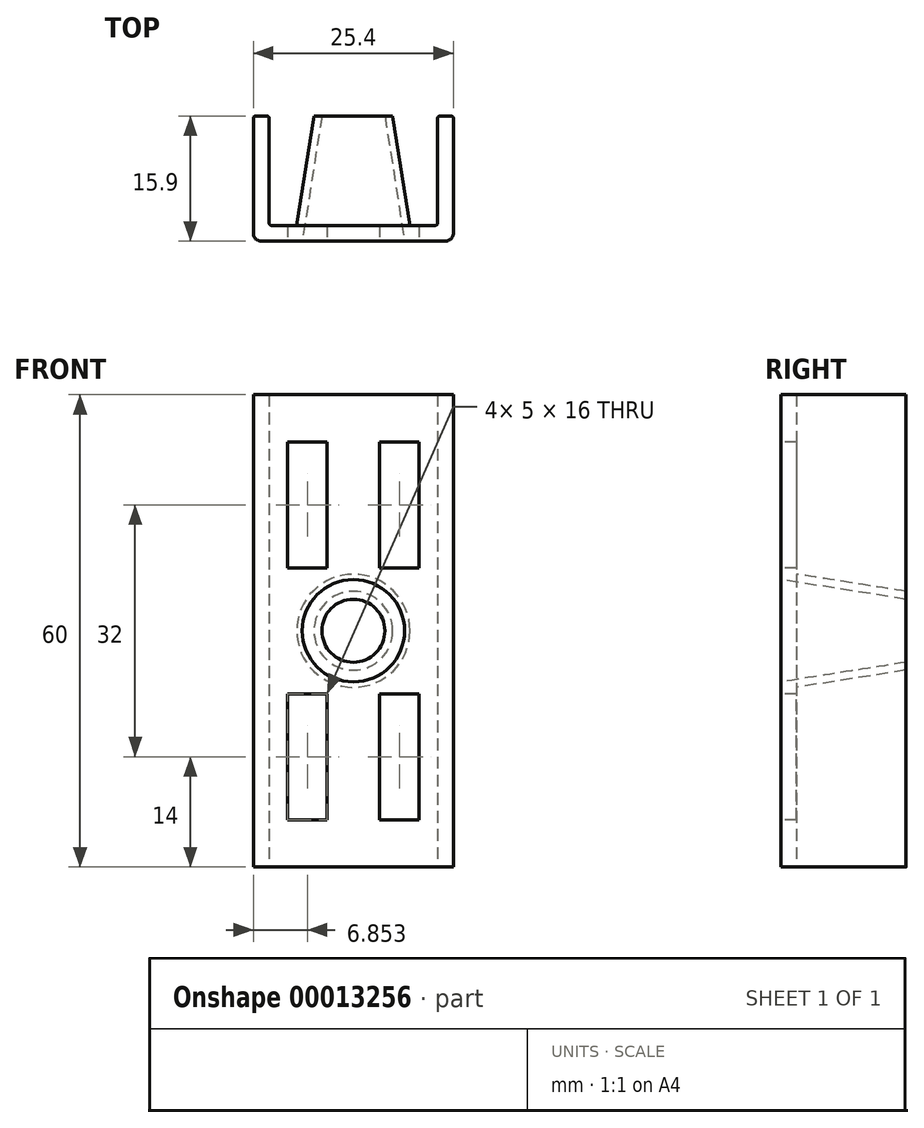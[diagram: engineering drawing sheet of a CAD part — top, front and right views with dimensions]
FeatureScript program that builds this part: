
annotation { "Feature Type Name" : "Feature", "Feature Type Description" : "" }
export const myFeature = defineFeature(function(context is Context, id is Id, definition is map)
    precondition{}
    {
        {
            var Q0;
            Q0=qCreatedBy(makeId("Top.planeOp"),FACE);
            var sketch = newSketch(context, id + "F0", { "sketchPlane" : qUnion([Q0])});
            skLineSegment(sketch, "E0.bottom", {"start": v(2.94, 36.07) * mm, "end": v(4.94, 36.07) * mm});
            skLineSegment(sketch, "E0.top", {"start": v(3.94, 20.17) * mm, "end": v(27.34, 20.17) * mm});
            skLineSegment(sketch, "E0.left", {"start": v(2.94, 36.07) * mm, "end": v(2.94, 21.17) * mm});
            skLineSegment(sketch, "E0.right", {"start": v(28.34, 36.07) * mm, "end": v(28.34, 21.17) * mm});
            skPoint(sketch, "E1.visualSharp", {"position": v(2.94, 20.17) * mm});
            skArc(sketch, "E1.filletArc", {"start": v(2.94, 21.17) * mm, "mid": v(3.24, 20.46) * mm, "end": v(3.94, 20.17) * mm});
            skPoint(sketch, "E2.visualSharp", {"position": v(28.34, 20.17) * mm});
            skArc(sketch, "E2.filletArc", {"start": v(27.34, 20.17) * mm, "mid": v(28.05, 20.46) * mm, "end": v(28.34, 21.17) * mm});
            skLineSegment(sketch, "E3.0", {"start": v(26.34, 36.07) * mm, "end": v(26.34, 22.17) * mm});
            skLineSegment(sketch, "E3.1", {"start": v(4.94, 22.17) * mm, "end": v(26.34, 22.17) * mm});
            skLineSegment(sketch, "E3.2", {"start": v(4.94, 36.07) * mm, "end": v(4.94, 22.17) * mm});
            skLineSegment(sketch, "E4.trimOffspring", {"start": v(26.34, 36.07) * mm, "end": v(28.34, 36.07) * mm});
            skSolve(sketch);
        }
        {
            var Q0;
            Q0=makeQuery(id+"F0.imprint","IMPRINT",FACE,{"disambiguationData":[TD([[makeQuery(id+"F0.imprint","IMPRINT",EDGE,{"derivedFrom":sQuery(id+"F0.wireOp",EDGE,"E0.bottom")}),-1.0]])]});
            extrude(context, id + "F1", {"entities" : qUnion([Q0]), "depth" : 60 * mm});
        }
        {
            var Q0;
            Q0=makeQuery(id+"F1.opExtrude","SWEPT_FACE",FACE,{"disambiguationData":[OSD([sQuery(id+"F0.wireOp",EDGE,"E0.top")])]});
            var sketch = newSketch(context, id + "F2", { "sketchPlane" : qUnion([Q0])});
            skLineSegment(sketch, "E5", {"start": v(15.64, 60) * mm, "end": v(15.64, 0) * mm, "construction": true});
            skLineSegment(sketch, "E6.bottom", {"start": v(19, 22) * mm, "end": v(24, 22) * mm});
            skLineSegment(sketch, "E6.top", {"start": v(19, 6) * mm, "end": v(24, 6) * mm});
            skLineSegment(sketch, "E6.left", {"start": v(19, 22) * mm, "end": v(19, 6) * mm});
            skLineSegment(sketch, "E6.right", {"start": v(24, 22) * mm, "end": v(24, 6) * mm});
            skLineSegment(sketch, "E7", {"start": v(15.64, 30) * mm, "end": v(27.34, 30) * mm, "construction": true});
            skLineSegment(sketch, "E8.0", {"start": v(15.64, 22) * mm, "end": v(27.34, 22) * mm, "construction": true});
            skPoint(sketch, "E9", {"position": v(21.5, 22) * mm});
            skLineSegment(sketch, "E10.0.MirrorCS", {"start": v(12.3, 22) * mm, "end": v(12.3, 6) * mm});
            skLineSegment(sketch, "E11.0.MirrorCS", {"start": v(7.3, 22) * mm, "end": v(7.3, 6) * mm});
            skLineSegment(sketch, "E12.0.MirrorCS", {"start": v(12.3, 22) * mm, "end": v(7.3, 22) * mm});
            skLineSegment(sketch, "E13.0.MirrorCS", {"start": v(12.3, 6) * mm, "end": v(7.3, 6) * mm});
            skLineSegment(sketch, "E14.0.MirrorCS", {"start": v(19, 38) * mm, "end": v(24, 38) * mm});
            skLineSegment(sketch, "E15.0.MirrorCS", {"start": v(24, 38) * mm, "end": v(24, 54) * mm});
            skLineSegment(sketch, "E16.0.MirrorCS", {"start": v(19, 38) * mm, "end": v(19, 54) * mm});
            skLineSegment(sketch, "E17.0.MirrorCS", {"start": v(19, 54) * mm, "end": v(24, 54) * mm});
            skLineSegment(sketch, "E18.0.MirrorCS", {"start": v(12.3, 38) * mm, "end": v(7.3, 38) * mm});
            skLineSegment(sketch, "E19.0.MirrorCS", {"start": v(12.3, 38) * mm, "end": v(12.3, 54) * mm});
            skLineSegment(sketch, "E20.0.MirrorCS", {"start": v(12.3, 54) * mm, "end": v(7.3, 54) * mm});
            skLineSegment(sketch, "E21.0.MirrorCS", {"start": v(7.3, 38) * mm, "end": v(7.3, 54) * mm});
            skCircle(sketch, "E22", {"center": v(15.64, 30) * mm, "radius": 7.5 * mm});
            skSolve(sketch);
        }
        {
            var Q0;
            Q0=makeQuery(id+"F2.imprint","IMPRINT",FACE,{"disambiguationData":[TD([[makeQuery(id+"F2.imprint","IMPRINT",EDGE,{"derivedFrom":sQuery(id+"F2.wireOp",EDGE,"E18.0.MirrorCS")}),-1.0]])]});
            var Q1;
            Q1=makeQuery(id+"F2.imprint","IMPRINT",FACE,{"disambiguationData":[TD([[makeQuery(id+"F2.imprint","IMPRINT",EDGE,{"derivedFrom":sQuery(id+"F2.wireOp",EDGE,"E14.0.MirrorCS")}),1.0]])]});
            var Q2;
            Q2=makeQuery(id+"F2.imprint","IMPRINT",FACE,{"disambiguationData":[TD([[makeQuery(id+"F2.imprint","IMPRINT",EDGE,{"derivedFrom":sQuery(id+"F2.wireOp",EDGE,"E6.bottom")}),-1.0]])]});
            var Q3;
            Q3=makeQuery(id+"F2.imprint","IMPRINT",FACE,{"disambiguationData":[TD([[makeQuery(id+"F2.imprint","IMPRINT",EDGE,{"derivedFrom":sQuery(id+"F2.wireOp",EDGE,"E10.0.MirrorCS")}),-1.0]])]});
            extrude(context, id + "F3", {"entities" : qUnion([Q0, Q1, Q2, Q3]), "operationType" : NewBodyOperationType.REMOVE, "oppositeDirection" : true, "depth" : 5 * mm});
        }
        {
            var Q0;
            Q0=makeQuery(id+"F1.opExtrude","SWEPT_EDGE",EDGE,{"disambiguationData":[OSD([sQuery(id+"F0.wireOp",EDGE,"E0.bottom"),sQuery(id+"F0.wireOp",EDGE,"E0.left")])]});
            var Q1;
            Q1=makeQuery(id+"F1.opExtrude","SWEPT_EDGE",EDGE,{"disambiguationData":[OSD([sQuery(id+"F0.wireOp",EDGE,"E0.bottom"),sQuery(id+"F0.wireOp",EDGE,"E3.2")])]});
            var Q2;
            Q2=makeQuery(id+"F1.opExtrude","SWEPT_EDGE",EDGE,{"disambiguationData":[OSD([sQuery(id+"F0.wireOp",EDGE,"E3.0"),sQuery(id+"F0.wireOp",EDGE,"E4.trimOffspring")])]});
            var Q3;
            Q3=makeQuery(id+"F1.opExtrude","SWEPT_EDGE",EDGE,{"disambiguationData":[OSD([sQuery(id+"F0.wireOp",EDGE,"E0.right"),sQuery(id+"F0.wireOp",EDGE,"E4.trimOffspring")])]});
            var Q4;
            Q4=makeQuery(id+"F1.opExtrude","SWEPT_EDGE",EDGE,{"disambiguationData":[OSD([sQuery(id+"F0.wireOp",EDGE,"E3.1"),sQuery(id+"F0.wireOp",EDGE,"E3.2")])]});
            var Q5;
            Q5=makeQuery(id+"F1.opExtrude","SWEPT_EDGE",EDGE,{"disambiguationData":[OSD([sQuery(id+"F0.wireOp",EDGE,"E3.0"),sQuery(id+"F0.wireOp",EDGE,"E3.1")])]});
            fillet(context, id + "F4", {"entities" : qUnion([Q0, Q1, Q2, Q3, Q4, Q5]), "radius" : 0.3 * mm, "tangentPropagation" : true, "allowEdgeOverflow" : false});
        }
        {
            var Q0;
            Q0=makeQuery(id+"F1.opExtrude","SWEPT_FACE",FACE,{"disambiguationData":[OSD([sQuery(id+"F0.wireOp",EDGE,"E0.bottom")])]});
            var sketch = newSketch(context, id + "F5", { "sketchPlane" : qUnion([Q0])});
            skLineSegment(sketch, "E23", {"start": v(-4.64, -7.56) * mm, "end": v(-26.64, -7.56) * mm, "construction": true});
            skPoint(sketch, "E24", {"position": v(-15.64, -7.56) * mm});
            skLineSegment(sketch, "E25", {"start": v(7.4, 0) * mm, "end": v(7.4, 60) * mm, "construction": true});
            skPoint(sketch, "E26", {"position": v(7.4, 30) * mm});
            skCircle(sketch, "E27", {"center": v(-15.64, 30) * mm, "radius": 5 * mm});
            skSolve(sketch);
        }
        {
            var Q1;
            Q1=makeQuery(id+"F5.imprint","IMPRINT",FACE,{"disambiguationData":[TD([[makeQuery(id+"F5.imprint","IMPRINT",EDGE,{"derivedFrom":sQuery(id+"F5.wireOp",EDGE,"E27")}),1.0]])]});
            var Q2;
            Q2=makeQuery(id+"F2.imprint","IMPRINT",FACE,{"disambiguationData":[TD([[makeQuery(id+"F2.imprint","IMPRINT",EDGE,{"derivedFrom":sQuery(id+"F2.wireOp",EDGE,"E22")}),1.0]])]});
            loft(context, id + "F6", {"operationType" : NewBodyOperationType.ADD, "sheetProfilesArray" : [{ "sheetProfileEntities" : qUnion([Q1]) }, { "sheetProfileEntities" : qUnion([Q2]) }]});
        }
        {
            var Q0;
            Q0=makeQuery(id+"F5.imprint","IMPRINT",FACE,{"disambiguationData":[TD([[makeQuery(id+"F5.imprint","IMPRINT",EDGE,{"derivedFrom":sQuery(id+"F5.wireOp",EDGE,"E27")}),1.0]])]});
            var sketch = newSketch(context, id + "F7", { "sketchPlane" : qUnion([Q0])});
            skCircle(sketch, "E28", {"center": v(-15.64, 30) * mm, "radius": 4 * mm});
            skSolve(sketch);
        }
        {
            var Q0;
            Q0=makeQuery(id+"F2.imprint","IMPRINT",FACE,{"disambiguationData":[TD([[makeQuery(id+"F2.imprint","IMPRINT",EDGE,{"derivedFrom":sQuery(id+"F2.wireOp",EDGE,"E22")}),1.0]])]});
            var sketch = newSketch(context, id + "F8", { "sketchPlane" : qUnion([Q0])});
            skCircle(sketch, "E29", {"center": v(15.64, 30) * mm, "radius": 6.5 * mm});
            skSolve(sketch);
        }
        {
            var Q1;
            Q1=makeQuery(id+"F7.imprint","IMPRINT",FACE,{"disambiguationData":[TD([[makeQuery(id+"F7.imprint","IMPRINT",EDGE,{"derivedFrom":sQuery(id+"F7.wireOp",EDGE,"E28")}),1.0]])]});
            var Q2;
            Q2=makeQuery(id+"F8.imprint","IMPRINT",FACE,{"disambiguationData":[TD([[makeQuery(id+"F8.imprint","IMPRINT",EDGE,{"derivedFrom":sQuery(id+"F8.wireOp",EDGE,"E29")}),1.0]])]});
            loft(context, id + "F9", {"operationType" : NewBodyOperationType.REMOVE, "sheetProfilesArray" : [{ "sheetProfileEntities" : qUnion([Q1]) }, { "sheetProfileEntities" : qUnion([Q2]) }]});
        }
    });
